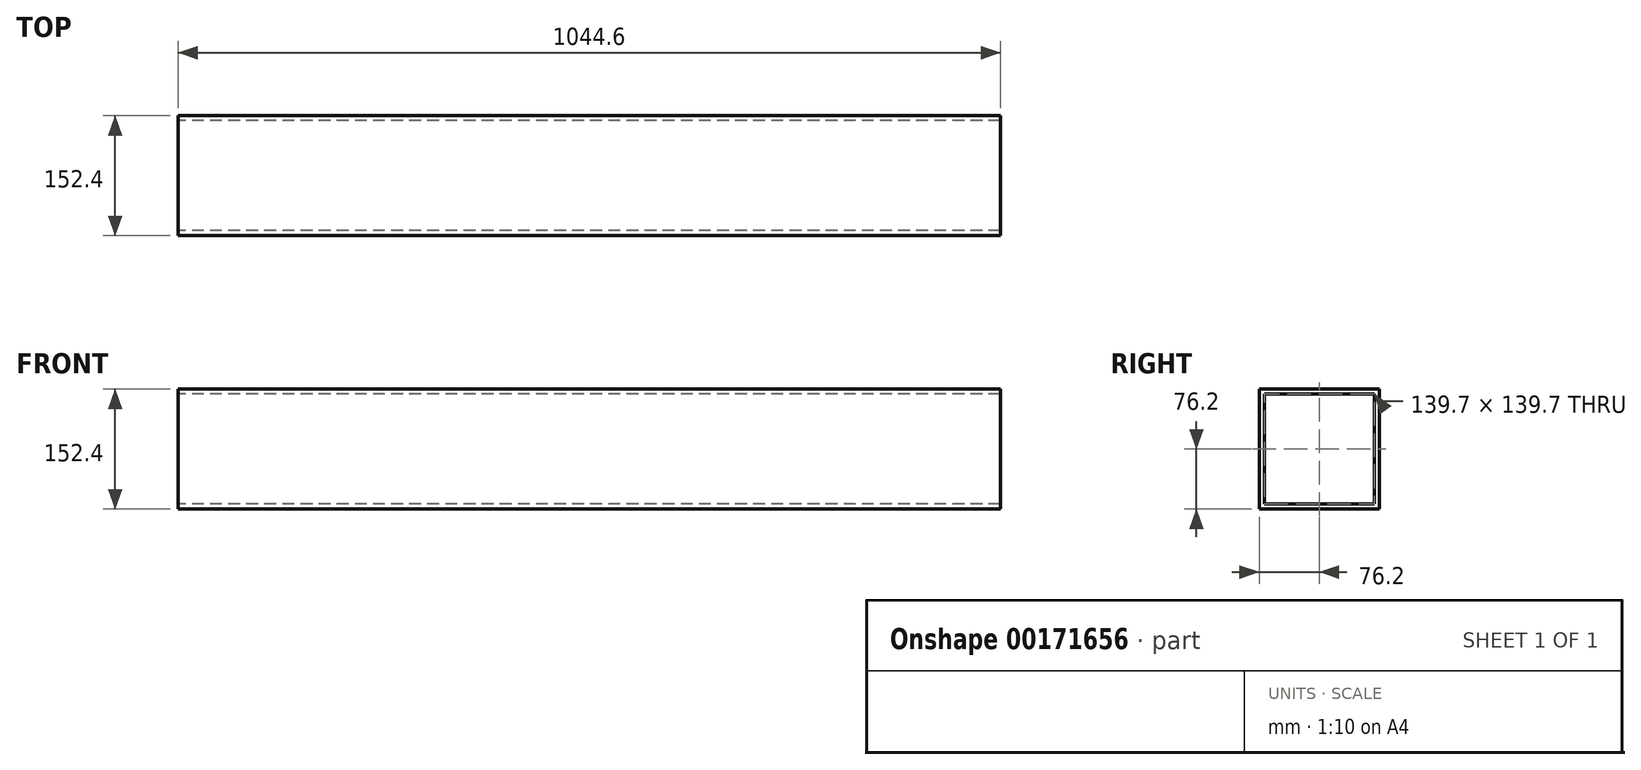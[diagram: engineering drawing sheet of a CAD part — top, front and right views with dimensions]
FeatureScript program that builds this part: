
annotation { "Feature Type Name" : "Feature", "Feature Type Description" : "" }
export const myFeature = defineFeature(function(context is Context, id is Id, definition is map)
    precondition{}
    {
        {
            var Q0;
            Q0=qCreatedBy(makeId("Right.planeOp"),FACE);
            var sketch = newSketch(context, id + "F0", { "sketchPlane" : qUnion([Q0])});
            skLineSegment(sketch, "E0.bottom", {"start": v(-76.2, 76.2) * mm, "end": v(76.2, 76.2) * mm});
            skLineSegment(sketch, "E0.top", {"start": v(-76.2, -76.2) * mm, "end": v(76.2, -76.2) * mm});
            skLineSegment(sketch, "E0.left", {"start": v(-76.2, 76.2) * mm, "end": v(-76.2, -76.2) * mm});
            skLineSegment(sketch, "E0.right", {"start": v(76.2, 76.2) * mm, "end": v(76.2, -76.2) * mm});
            skLineSegment(sketch, "E1.bottom", {"start": v(-69.85, 69.85) * mm, "end": v(69.85, 69.85) * mm});
            skLineSegment(sketch, "E1.top", {"start": v(-69.85, -69.85) * mm, "end": v(69.85, -69.85) * mm});
            skLineSegment(sketch, "E1.left", {"start": v(-69.85, 69.85) * mm, "end": v(-69.85, -69.85) * mm});
            skLineSegment(sketch, "E1.right", {"start": v(69.85, 69.85) * mm, "end": v(69.85, -69.85) * mm});
            skSolve(sketch);
        }
        {
            var Q0;
            Q0=makeQuery(id+"F0.imprint","IMPRINT",FACE,{"disambiguationData":[TD([[makeQuery(id+"F0.imprint","IMPRINT",EDGE,{"derivedFrom":sQuery(id+"F0.wireOp",EDGE,"E0.bottom")}),-1.0]])]});
            extrude(context, id + "F1", {"entities" : qUnion([Q0]), "depth" : 1044.6 * mm});
        }
    });
